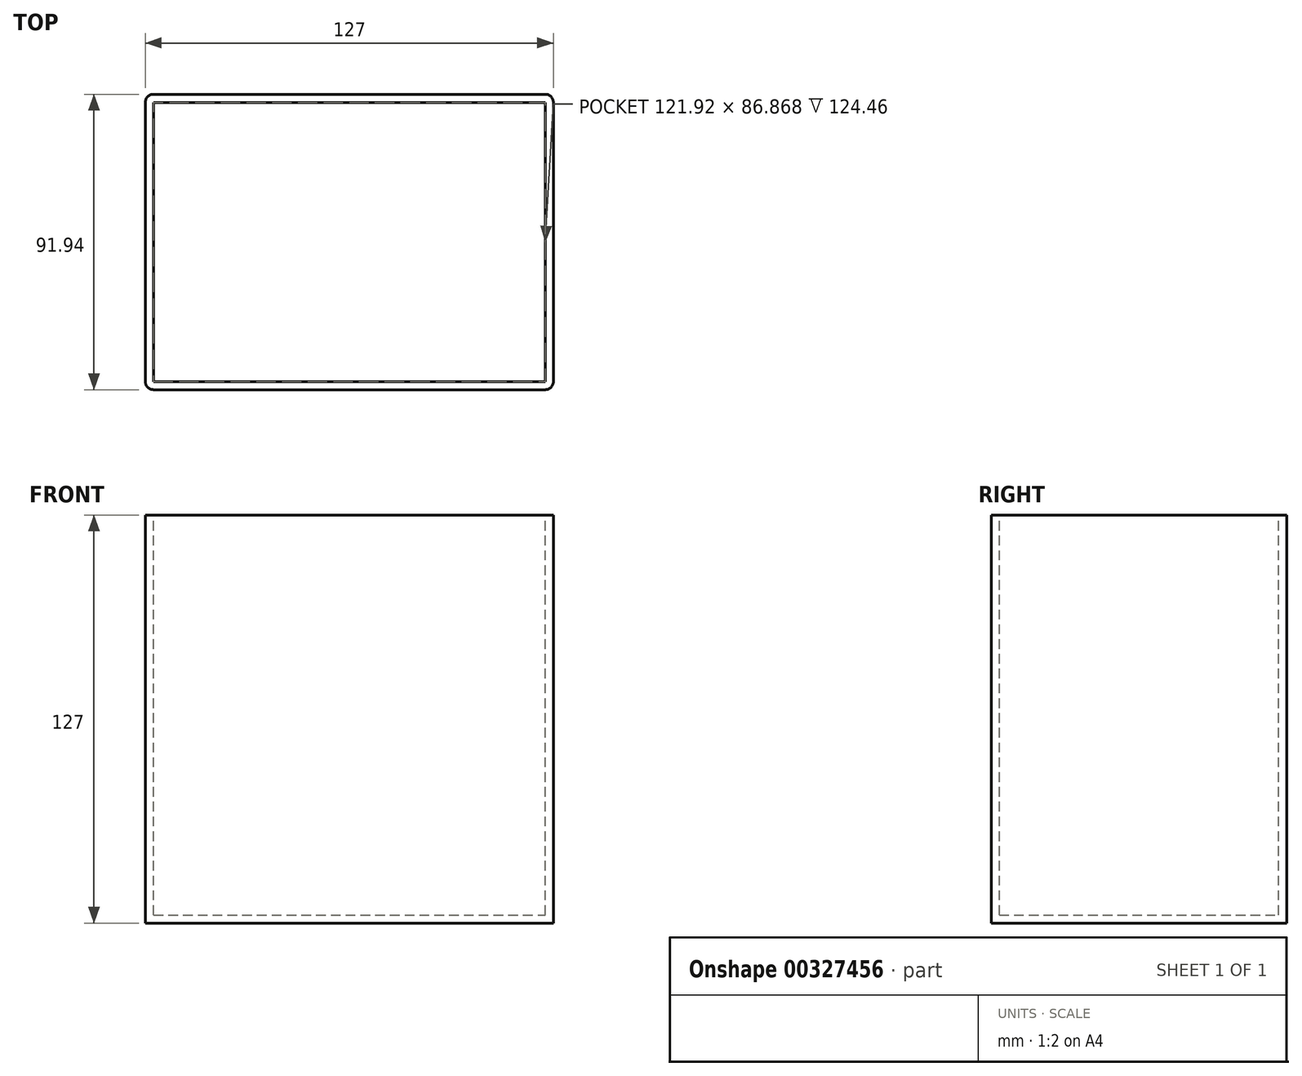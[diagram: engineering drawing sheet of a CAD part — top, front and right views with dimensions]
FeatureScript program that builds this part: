
annotation { "Feature Type Name" : "Feature", "Feature Type Description" : "" }
export const myFeature = defineFeature(function(context is Context, id is Id, definition is map)
    precondition{}
    {
        {
            var Q0;
            Q0=qCreatedBy(makeId("Front.planeOp"),FACE);
            var sketch = newSketch(context, id + "F0", { "sketchPlane" : qUnion([Q0])});
            skLineSegment(sketch, "E0.bottom", {"start": v(-63.95, 127) * mm, "end": v(63.05, 127) * mm});
            skLineSegment(sketch, "E0.top", {"start": v(-63.95, 0) * mm, "end": v(63.05, 0) * mm});
            skLineSegment(sketch, "E0.left", {"start": v(-63.95, 127) * mm, "end": v(-63.95, 0) * mm});
            skLineSegment(sketch, "E0.right", {"start": v(63.05, 127) * mm, "end": v(63.05, 0) * mm});
            skSolve(sketch);
        }
        {
            var Q0;
            Q0=makeQuery(id+"F0.imprint","IMPRINT",FACE,{"disambiguationData":[TD([[makeQuery(id+"F0.imprint","IMPRINT",EDGE,{"derivedFrom":sQuery(id+"F0.wireOp",EDGE,"E0.bottom")}),-1.0]])]});
            extrude(context, id + "F1", {"entities" : qUnion([Q0]), "endBound" : BoundingType.SYMMETRIC, "depth" : 91.95 * mm});
        }
        {
            var Q0;
            Q0=makeQuery(id+"F1.opExtrude","CAP_EDGE",EDGE,{"disambiguationData":[OSD([sQuery(id+"F0.wireOp",EDGE,"E0.left")])],"isStart":false});
            var Q1;
            Q1=makeQuery(id+"F1.opExtrude","CAP_EDGE",EDGE,{"disambiguationData":[OSD([sQuery(id+"F0.wireOp",EDGE,"E0.right")])],"isStart":false});
            var Q2;
            Q2=makeQuery(id+"F1.opExtrude","CAP_EDGE",EDGE,{"disambiguationData":[OSD([sQuery(id+"F0.wireOp",EDGE,"E0.right")])],"isStart":true});
            var Q3;
            Q3=makeQuery(id+"F1.opExtrude","CAP_EDGE",EDGE,{"disambiguationData":[OSD([sQuery(id+"F0.wireOp",EDGE,"E0.left")])],"isStart":true});
            fillet(context, id + "F2", {"entities" : qUnion([Q0, Q1, Q2, Q3]), "radius" : 2.54 * mm, "tangentPropagation" : true, "allowEdgeOverflow" : false});
        }
        {
            var Q0;
            Q0=makeQuery(id+"F1.opExtrude","SWEPT_FACE",FACE,{"disambiguationData":[OSD([sQuery(id+"F0.wireOp",EDGE,"E0.bottom")])]});
            shell(context, id + "F3", {"entities" : qUnion([Q0]), "thickness" : 2.54 * mm});
        }
    });
